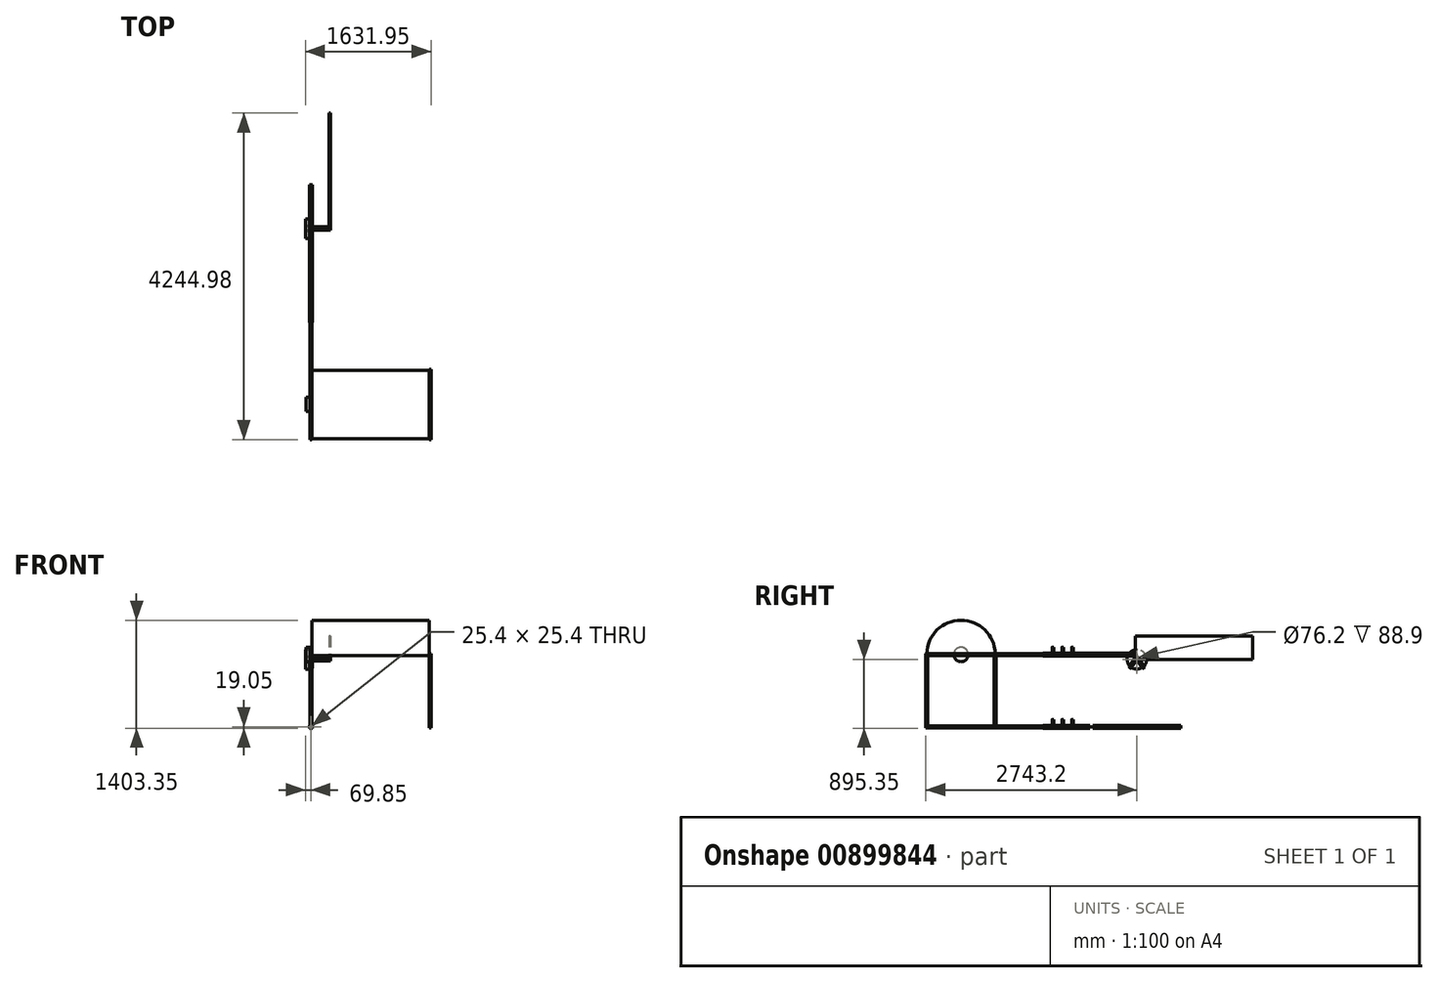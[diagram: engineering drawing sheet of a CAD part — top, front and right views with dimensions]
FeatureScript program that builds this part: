
annotation { "Feature Type Name" : "Feature", "Feature Type Description" : "" }
export const myFeature = defineFeature(function(context is Context, id is Id, definition is map)
    precondition{}
    {
        {
            var Q0;
            Q0=qCreatedBy(makeId("Top.planeOp"),FACE);
            var sketch = newSketch(context, id + "F0", { "sketchPlane" : qUnion([Q0])});
            skLineSegment(sketch, "E0.bottom", {"start": v(0, -232.23) * mm, "end": v(-25.4, -232.23) * mm});
            skLineSegment(sketch, "E0.top", {"start": v(0, 682.17) * mm, "end": v(-25.4, 682.17) * mm});
            skLineSegment(sketch, "E0.left", {"start": v(0, -232.23) * mm, "end": v(0, 682.17) * mm});
            skLineSegment(sketch, "E0.right", {"start": v(-25.4, -232.23) * mm, "end": v(-25.4, 682.17) * mm});
            skLineSegment(sketch, "E1", {"start": v(0, -232.23) * mm, "end": v(1524, -232.23) * mm});
            skLineSegment(sketch, "E2.bottom", {"start": v(1524, -232.23) * mm, "end": v(1549.4, -232.23) * mm});
            skLineSegment(sketch, "E2.top", {"start": v(1524, 682.17) * mm, "end": v(1549.4, 682.17) * mm});
            skLineSegment(sketch, "E2.left", {"start": v(1524, -232.23) * mm, "end": v(1524, 682.17) * mm});
            skLineSegment(sketch, "E2.right", {"start": v(1549.4, -232.23) * mm, "end": v(1549.4, 682.17) * mm});
            skSolve(sketch);
        }
        {
            var Q0;
            Q0=makeQuery(id+"F0.imprint","IMPRINT",FACE,{"disambiguationData":[TD([[makeQuery(id+"F0.imprint","IMPRINT",EDGE,{"derivedFrom":sQuery(id+"F0.wireOp",EDGE,"E0.bottom")}),-1.0]])]});
            var Q1;
            Q1=makeQuery(id+"F0.imprint","IMPRINT",FACE,{"disambiguationData":[TD([[makeQuery(id+"F0.imprint","IMPRINT",EDGE,{"derivedFrom":sQuery(id+"F0.wireOp",EDGE,"E2.bottom")}),1.0]])]});
            extrude(context, id + "F1", {"entities" : qUnion([Q0, Q1]), "depth" : 25.4 * mm, "offsetDistance" : 25.4 * mm});
        }
        {
            var Q0;
            Q0=makeQuery(id+"F1.opExtrude","CAP_FACE",FACE,{"disambiguationData":[OSD([sQuery(id+"F0.wireOp",EDGE,"E0.bottom"),sQuery(id+"F0.wireOp",EDGE,"E0.top"),sQuery(id+"F0.wireOp",EDGE,"E0.left"),sQuery(id+"F0.wireOp",EDGE,"E0.right")])],"isStart":false});
            var sketch = newSketch(context, id + "F2", { "sketchPlane" : qUnion([Q0])});
            skLineSegment(sketch, "E3.bottom", {"start": v(0, -232.23) * mm, "end": v(-25.4, -232.23) * mm});
            skLineSegment(sketch, "E3.top", {"start": v(0, -206.83) * mm, "end": v(-25.4, -206.83) * mm});
            skLineSegment(sketch, "E3.left", {"start": v(0, -232.23) * mm, "end": v(0, -206.83) * mm});
            skLineSegment(sketch, "E3.right", {"start": v(-25.4, -232.23) * mm, "end": v(-25.4, -206.83) * mm});
            skLineSegment(sketch, "E4.bottom", {"start": v(-25.4, 682.17) * mm, "end": v(0, 682.17) * mm});
            skLineSegment(sketch, "E4.top", {"start": v(-25.4, 656.77) * mm, "end": v(0, 656.77) * mm});
            skLineSegment(sketch, "E4.left", {"start": v(-25.4, 682.17) * mm, "end": v(-25.4, 656.77) * mm});
            skLineSegment(sketch, "E4.right", {"start": v(0, 682.17) * mm, "end": v(0, 656.77) * mm});
            skSolve(sketch);
        }
        {
            var Q0;
            Q0=makeQuery(id+"F1.opExtrude","CAP_FACE",FACE,{"disambiguationData":[OSD([sQuery(id+"F0.wireOp",EDGE,"E2.bottom"),sQuery(id+"F0.wireOp",EDGE,"E2.top"),sQuery(id+"F0.wireOp",EDGE,"E2.left"),sQuery(id+"F0.wireOp",EDGE,"E2.right")])],"isStart":false});
            var sketch = newSketch(context, id + "F3", { "sketchPlane" : qUnion([Q0])});
            skLineSegment(sketch, "E5.bottom", {"start": v(1524, 682.17) * mm, "end": v(1549.4, 682.17) * mm});
            skLineSegment(sketch, "E5.top", {"start": v(1524, 656.77) * mm, "end": v(1549.4, 656.77) * mm});
            skLineSegment(sketch, "E5.left", {"start": v(1524, 682.17) * mm, "end": v(1524, 656.77) * mm});
            skLineSegment(sketch, "E5.right", {"start": v(1549.4, 682.17) * mm, "end": v(1549.4, 656.77) * mm});
            skLineSegment(sketch, "E6.bottom", {"start": v(1549.4, -232.23) * mm, "end": v(1524, -232.23) * mm});
            skLineSegment(sketch, "E6.top", {"start": v(1549.4, -206.83) * mm, "end": v(1524, -206.83) * mm});
            skLineSegment(sketch, "E6.left", {"start": v(1549.4, -232.23) * mm, "end": v(1549.4, -206.83) * mm});
            skLineSegment(sketch, "E6.right", {"start": v(1524, -232.23) * mm, "end": v(1524, -206.83) * mm});
            skSolve(sketch);
        }
        {
            var Q0;
            Q0=makeQuery(id+"F2.imprint","IMPRINT",FACE,{"disambiguationData":[TD([[makeQuery(id+"F2.imprint","IMPRINT",EDGE,{"derivedFrom":sQuery(id+"F2.wireOp",EDGE,"E4.bottom")}),1.0]])]});
            var Q1;
            Q1=makeQuery(id+"F2.imprint","IMPRINT",FACE,{"disambiguationData":[TD([[makeQuery(id+"F2.imprint","IMPRINT",EDGE,{"derivedFrom":sQuery(id+"F2.wireOp",EDGE,"E3.bottom")}),-1.0]])]});
            var Q2;
            Q2=makeQuery(id+"F3.imprint","IMPRINT",FACE,{"disambiguationData":[TD([[makeQuery(id+"F3.imprint","IMPRINT",EDGE,{"derivedFrom":sQuery(id+"F3.wireOp",EDGE,"E6.bottom")}),1.0]])]});
            var Q3;
            Q3=makeQuery(id+"F3.imprint","IMPRINT",FACE,{"disambiguationData":[TD([[makeQuery(id+"F3.imprint","IMPRINT",EDGE,{"derivedFrom":sQuery(id+"F3.wireOp",EDGE,"E5.bottom")}),-1.0]])]});
            extrude(context, id + "F4", {"entities" : qUnion([Q0, Q1, Q2, Q3]), "depth" : 914.4 * mm, "offsetDistance" : 25.4 * mm});
        }
        {
            var Q0;
            Q0=makeQuery(id+"F4.opExtrude","CAP_FACE",FACE,{"disambiguationData":[OSD([sQuery(id+"F2.wireOp",EDGE,"E3.bottom"),sQuery(id+"F2.wireOp",EDGE,"E3.top"),sQuery(id+"F2.wireOp",EDGE,"E3.left"),sQuery(id+"F2.wireOp",EDGE,"E3.right")])],"isStart":false});
            var sketch = newSketch(context, id + "F5", { "sketchPlane" : qUnion([Q0])});
            skLineSegment(sketch, "E7.bottom", {"start": v(0, -232.23) * mm, "end": v(-25.4, -232.23) * mm});
            skLineSegment(sketch, "E7.top", {"start": v(0, 682.17) * mm, "end": v(-25.4, 682.17) * mm});
            skLineSegment(sketch, "E7.left", {"start": v(0, -232.23) * mm, "end": v(0, 682.17) * mm});
            skLineSegment(sketch, "E7.right", {"start": v(-25.4, -232.23) * mm, "end": v(-25.4, 682.17) * mm});
            skSolve(sketch);
        }
        {
            var Q0;
            Q0=makeQuery(id+"F4.opExtrude","CAP_FACE",FACE,{"disambiguationData":[OSD([sQuery(id+"F3.wireOp",EDGE,"E6.bottom"),sQuery(id+"F3.wireOp",EDGE,"E6.top"),sQuery(id+"F3.wireOp",EDGE,"E6.left"),sQuery(id+"F3.wireOp",EDGE,"E6.right")])],"isStart":false});
            var sketch = newSketch(context, id + "F6", { "sketchPlane" : qUnion([Q0])});
            skLineSegment(sketch, "E8.bottom", {"start": v(1549.4, -232.23) * mm, "end": v(1524, -232.23) * mm});
            skLineSegment(sketch, "E8.top", {"start": v(1549.4, 682.17) * mm, "end": v(1524, 682.17) * mm});
            skLineSegment(sketch, "E8.left", {"start": v(1549.4, -232.23) * mm, "end": v(1549.4, 682.17) * mm});
            skLineSegment(sketch, "E8.right", {"start": v(1524, -232.23) * mm, "end": v(1524, 682.17) * mm});
            skSolve(sketch);
        }
        {
            var Q0;
            {var subQ0=sQuery(id+"F6.wireOp",EDGE,"E8.bottom");Q0=makeQuery(id+"F6.imprint","IMPRINT",FACE,{"disambiguationData":[TD([[makeQuery(id+"F6.imprint","IMPRINT",EDGE,{"derivedFrom":subQ0}),1.0]])]});}
            var Q1;
            {var subQ0=sQuery(id+"F6.wireOp",EDGE,"E8.top");Q1=makeQuery(id+"F6.imprint","IMPRINT",FACE,{"disambiguationData":[TD([[makeQuery(id+"F6.imprint","IMPRINT",EDGE,{"derivedFrom":subQ0}),1.0]])]});}
            var Q2;
            {var subQ0=sQuery(id+"F5.wireOp",EDGE,"E7.bottom");Q2=makeQuery(id+"F5.imprint","IMPRINT",FACE,{"disambiguationData":[TD([[makeQuery(id+"F5.imprint","IMPRINT",EDGE,{"derivedFrom":subQ0}),-1.0]])]});}
            var Q3;
            {var subQ0=sQuery(id+"F5.wireOp",EDGE,"E7.top");Q3=makeQuery(id+"F5.imprint","IMPRINT",FACE,{"disambiguationData":[TD([[makeQuery(id+"F5.imprint","IMPRINT",EDGE,{"derivedFrom":subQ0}),1.0]])]});}
            extrude(context, id + "F7", {"entities" : qUnion([Q0, Q1, Q2, Q3]), "depth" : 25.4 * mm, "offsetDistance" : 25.4 * mm});
        }
        {
            var Q0;
            Q0=makeQuery(id+"F7.opExtrude","SWEPT_FACE",FACE,{"disambiguationData":[OSD([sQuery(id+"F5.wireOp",EDGE,"E7.left")])]});
            var sketch = newSketch(context, id + "F8", { "sketchPlane" : qUnion([Q0])});
            skLineSegment(sketch, "E9", {"start": v(-232.23, 965.2) * mm, "end": v(224.97, 965.2) * mm});
            skLineSegment(sketch, "E10", {"start": v(224.97, 965.2) * mm, "end": v(682.17, 965.2) * mm});
            skLineSegment(sketch, "E11", {"start": v(-232.23, 965.2) * mm, "end": v(-232.23, 952.5) * mm});
            skLineSegment(sketch, "E12", {"start": v(-232.23, 952.5) * mm, "end": v(224.97, 952.5) * mm});
            skCircle(sketch, "E13", {"center": v(224.97, 952.5) * mm, "radius": 444.5 * mm});
            skSolve(sketch);
        }
        {
            var Q0;
            {var subQ0=sQuery(id+"F8.wireOp",EDGE,"E10");var subQ1=sQuery(id+"F8.wireOp",EDGE,"E9");var subQ2=makeQuery(id+"F8.imprint","INTERSECT",VERTEX,{"derivedFrom":[subQ1,subQ0]});Q0=makeQuery(id+"F8.imprint","IMPRINT",FACE,{"disambiguationData":[TD([[makeQuery(id+"F8.imprint","IMPRINT",EDGE,{"disambiguationData":[TD([[subQ2,1.0]])],"derivedFrom":subQ1}),1.0]])]});}
            var Q1;
            {var subQ4=sQuery(id+"F8.wireOp",EDGE,"E9");var subQ6=sQuery(id+"F8.wireOp",EDGE,"E10");var subQ7=makeQuery(id+"F8.imprint","INTERSECT",VERTEX,{"derivedFrom":[subQ4,subQ6]});Q1=makeQuery(id+"F8.imprint","IMPRINT",FACE,{"disambiguationData":[TD([[makeQuery(id+"F8.imprint","IMPRINT",EDGE,{"disambiguationData":[TD([[subQ7,1.0]])],"derivedFrom":subQ4}),-1.0]])]});}
            var Q2;
            {var subQ0=sQuery(id+"F8.wireOp",EDGE,"E13");var subQ1=makeQuery(id+"F7.opExtrude","CAP_EDGE",EDGE,{"disambiguationData":[OSD([sQuery(id+"F5.wireOp",EDGE,"E7.left")])],"isStart":true});var subQ2=makeQuery(id+"F8.imprint","INTERSECT",VERTEX,{"disambiguationData":[OD(0.0)],"derivedFrom":[subQ1,subQ0]});Q2=makeQuery(id+"F8.imprint","IMPRINT",FACE,{"disambiguationData":[TD([[makeQuery(id+"F8.imprint","IMPRINT",EDGE,{"disambiguationData":[TD([[subQ2,-1.0]])],"derivedFrom":subQ0}),1.0]])]});}
            extrude(context, id + "F9", {"entities" : qUnion([Q0, Q1, Q2]), "depth" : 1524 * mm, "offsetDistance" : 25.4 * mm});
        }
        {
            var Q0;
            Q0=makeQuery(id+"F7.opExtrude","SWEPT_FACE",FACE,{"disambiguationData":[OSD([sQuery(id+"F5.wireOp",EDGE,"E7.right")])]});
            var sketch = newSketch(context, id + "F10", { "sketchPlane" : qUnion([Q0])});
            skLineSegment(sketch, "E14", {"start": v(-682.17, 939.8) * mm, "end": v(-682.17, 952.5) * mm});
            skLineSegment(sketch, "E15", {"start": v(-682.17, 952.5) * mm, "end": v(-224.97, 952.5) * mm});
            skPoint(sketch, "E15.endSnap0", {"position": v(-224.97, 939.8) * mm});
            skCircle(sketch, "E16", {"center": v(-224.97, 952.5) * mm, "radius": 93.93 * mm});
            skSolve(sketch);
        }
        {
            var Q0;
            {var subQ0=sQuery(id+"F10.wireOp",EDGE,"E16");var subQ1=makeQuery(id+"F7.opExtrude","CAP_EDGE",EDGE,{"disambiguationData":[OSD([sQuery(id+"F5.wireOp",EDGE,"E7.right")])],"isStart":false});var subQ2=makeQuery(id+"F10.imprint","INTERSECT",VERTEX,{"disambiguationData":[OD(0.0)],"derivedFrom":[subQ1,subQ0]});Q0=makeQuery(id+"F10.imprint","IMPRINT",FACE,{"disambiguationData":[TD([[makeQuery(id+"F10.imprint","IMPRINT",EDGE,{"disambiguationData":[TD([[subQ2,1.0]])],"derivedFrom":subQ0}),1.0]])]});}
            var Q1;
            {var subQ0=sQuery(id+"F10.wireOp",EDGE,"E16");var subQ7=makeQuery(id+"F10.imprint","INTERSECT",VERTEX,{"derivedFrom":[sQuery(id+"F10.wireOp",EDGE,"E15"),subQ0]});Q1=makeQuery(id+"F10.imprint","IMPRINT",FACE,{"disambiguationData":[TD([[makeQuery(id+"F10.imprint","IMPRINT",EDGE,{"disambiguationData":[TD([[subQ7,1.0]])],"derivedFrom":subQ0}),1.0]])]});}
            var Q2;
            {var subQ0=sQuery(id+"F10.wireOp",EDGE,"E16");var subQ1=makeQuery(id+"F7.opExtrude","CAP_EDGE",EDGE,{"disambiguationData":[OSD([sQuery(id+"F5.wireOp",EDGE,"E7.right")])],"isStart":true});var subQ2=makeQuery(id+"F10.imprint","INTERSECT",VERTEX,{"disambiguationData":[OD(0.0)],"derivedFrom":[subQ1,subQ0]});Q2=makeQuery(id+"F10.imprint","IMPRINT",FACE,{"disambiguationData":[TD([[makeQuery(id+"F10.imprint","IMPRINT",EDGE,{"disambiguationData":[TD([[subQ2,-1.0]])],"derivedFrom":subQ0}),1.0]])]});}
            extrude(context, id + "F11", {"entities" : qUnion([Q0, Q1, Q2]), "operationType" : NewBodyOperationType.ADD, "depth" : 50.8 * mm, "offsetDistance" : 25.4 * mm});
        }
        {
            var Q0;
            Q0=makeQuery(id+"F1.opExtrude","SWEPT_FACE",FACE,{"disambiguationData":[OSD([sQuery(id+"F0.wireOp",EDGE,"E0.top")])]});
            extrude(context, id + "F12", {"entities" : qUnion([Q0]), "operationType" : NewBodyOperationType.ADD, "depth" : 609.6 * mm, "offsetDistance" : 25.4 * mm});
        }
        {
            var Q0;
            Q0=makeQuery(id+"F7.opExtrude","SWEPT_FACE",FACE,{"disambiguationData":[OSD([sQuery(id+"F5.wireOp",EDGE,"E7.top")])]});
            extrude(context, id + "F13", {"entities" : qUnion([Q0]), "operationType" : NewBodyOperationType.ADD, "depth" : 609.6 * mm, "offsetDistance" : 25.4 * mm});
        }
        {
            var Q0;
            Q0=makeQuery(id+"F13.opExtrude","CAP_FACE",FACE,{"disambiguationData":[OSD([sQuery(id+"F5.wireOp",EDGE,"E7.top")])],"isStart":false});
            var sketch = newSketch(context, id + "F14", { "sketchPlane" : qUnion([Q0])});
            skLineSegment(sketch, "E17", {"start": v(0, 952.5) * mm, "end": v(25.4, 952.5) * mm});
            skLineSegment(sketch, "E18", {"start": v(25.4, 952.5) * mm, "end": v(25.4, 939.8) * mm});
            skLineSegment(sketch, "E19", {"start": v(12.7, 939.8) * mm, "end": v(12.7, 965.2) * mm});
            skLineSegment(sketch, "E20.bottom", {"start": v(12.7, 952.5) * mm, "end": v(31.75, 952.5) * mm});
            skLineSegment(sketch, "E20.top", {"start": v(12.7, 971.55) * mm, "end": v(31.75, 971.55) * mm});
            skLineSegment(sketch, "E20.left", {"start": v(12.7, 952.5) * mm, "end": v(12.7, 971.55) * mm});
            skLineSegment(sketch, "E20.right", {"start": v(31.75, 952.5) * mm, "end": v(31.75, 971.55) * mm});
            skLineSegment(sketch, "E21.bottom", {"start": v(12.7, 952.5) * mm, "end": v(-6.35, 952.5) * mm});
            skLineSegment(sketch, "E21.top", {"start": v(12.7, 971.55) * mm, "end": v(-6.35, 971.55) * mm});
            skLineSegment(sketch, "E21.right", {"start": v(-6.35, 952.5) * mm, "end": v(-6.35, 971.55) * mm});
            skLineSegment(sketch, "E22.bottom", {"start": v(12.7, 952.5) * mm, "end": v(41.68, 952.5) * mm});
            skLineSegment(sketch, "E23.bottom", {"start": v(12.7, 952.5) * mm, "end": v(-25.57, 952.5) * mm});
            skLineSegment(sketch, "E24.bottom", {"start": v(-6.35, 952.5) * mm, "end": v(12.7, 952.5) * mm});
            skLineSegment(sketch, "E24.top", {"start": v(-6.35, 933.45) * mm, "end": v(12.7, 933.45) * mm});
            skLineSegment(sketch, "E24.left", {"start": v(-6.35, 952.5) * mm, "end": v(-6.35, 933.45) * mm});
            skLineSegment(sketch, "E24.right", {"start": v(12.7, 952.5) * mm, "end": v(12.7, 933.45) * mm});
            skLineSegment(sketch, "E25.top", {"start": v(12.7, 933.45) * mm, "end": v(31.75, 933.45) * mm});
            skLineSegment(sketch, "E25.right", {"start": v(31.75, 952.5) * mm, "end": v(31.75, 933.45) * mm});
            skSolve(sketch);
        }
        {
            var Q0;
            {var subQ6=sQuery(id+"F14.wireOp",EDGE,"E21.top");Q0=makeQuery(id+"F14.imprint","IMPRINT",FACE,{"disambiguationData":[TD([[makeQuery(id+"F14.imprint","IMPRINT",EDGE,{"derivedFrom":subQ6}),1.0]])]});}
            var Q1;
            {var subQ1=sQuery(id+"F14.wireOp",EDGE,"E20.top");Q1=makeQuery(id+"F14.imprint","IMPRINT",FACE,{"disambiguationData":[TD([[makeQuery(id+"F14.imprint","IMPRINT",EDGE,{"derivedFrom":subQ1}),-1.0]])]});}
            var Q2;
            {var subQ2=sQuery(id+"F14.wireOp",EDGE,"E18");Q2=makeQuery(id+"F14.imprint","IMPRINT",FACE,{"disambiguationData":[TD([[makeQuery(id+"F14.imprint","IMPRINT",EDGE,{"derivedFrom":subQ2}),1.0]])]});}
            var Q3;
            {var subQ1=sQuery(id+"F14.wireOp",EDGE,"E24.top");Q3=makeQuery(id+"F14.imprint","IMPRINT",FACE,{"disambiguationData":[TD([[makeQuery(id+"F14.imprint","IMPRINT",EDGE,{"derivedFrom":subQ1}),1.0]])]});}
            extrude(context, id + "F15", {"entities" : qUnion([Q0, Q1, Q2, Q3]), "depth" : 1219.2 * mm, "offsetDistance" : 25.4 * mm});
        }
        {
            var Q0;
            Q0=makeQuery(id+"F12.opExtrude","CAP_FACE",FACE,{"disambiguationData":[OSD([sQuery(id+"F0.wireOp",EDGE,"E0.top")])],"isStart":false});
            var sketch = newSketch(context, id + "F16", { "sketchPlane" : qUnion([Q0])});
            skLineSegment(sketch, "E26", {"start": v(0, 25.4) * mm, "end": v(12.7, 25.4) * mm});
            skLineSegment(sketch, "E27", {"start": v(12.7, 25.4) * mm, "end": v(12.7, 12.7) * mm});
            skPoint(sketch, "E27.endSnap0", {"position": v(0, 12.7) * mm});
            skLineSegment(sketch, "E28", {"start": v(12.7, 12.7) * mm, "end": v(0, 12.7) * mm});
            skLineSegment(sketch, "E29.bottom", {"start": v(12.7, 12.7) * mm, "end": v(-6.35, 12.7) * mm});
            skLineSegment(sketch, "E29.top", {"start": v(12.7, 31.75) * mm, "end": v(-6.35, 31.75) * mm});
            skLineSegment(sketch, "E29.left", {"start": v(12.7, 12.7) * mm, "end": v(12.7, 31.75) * mm});
            skLineSegment(sketch, "E29.right", {"start": v(-6.35, 12.7) * mm, "end": v(-6.35, 31.75) * mm});
            skLineSegment(sketch, "E30.bottom", {"start": v(12.7, 12.7) * mm, "end": v(31.75, 12.7) * mm});
            skLineSegment(sketch, "E30.top", {"start": v(12.7, -6.35) * mm, "end": v(31.75, -6.35) * mm});
            skLineSegment(sketch, "E30.left", {"start": v(12.7, 12.7) * mm, "end": v(12.7, -6.35) * mm});
            skLineSegment(sketch, "E30.right", {"start": v(31.75, 12.7) * mm, "end": v(31.75, -6.35) * mm});
            skLineSegment(sketch, "E31.top", {"start": v(12.7, 31.75) * mm, "end": v(31.75, 31.75) * mm});
            skLineSegment(sketch, "E31.right", {"start": v(31.75, 12.7) * mm, "end": v(31.75, 31.75) * mm});
            skLineSegment(sketch, "E32.top", {"start": v(12.7, -6.35) * mm, "end": v(-6.35, -6.35) * mm});
            skLineSegment(sketch, "E32.right", {"start": v(-6.35, 12.7) * mm, "end": v(-6.35, -6.35) * mm});
            skSolve(sketch);
        }
        {
            var Q0;
            {var subQ1=sQuery(id+"F16.wireOp",EDGE,"E26");Q0=makeQuery(id+"F16.imprint","IMPRINT",FACE,{"disambiguationData":[TD([[makeQuery(id+"F16.imprint","IMPRINT",EDGE,{"derivedFrom":subQ1}),1.0]])]});}
            var Q1;
            {var subQ9=sQuery(id+"F16.wireOp",EDGE,"E31.top");Q1=makeQuery(id+"F16.imprint","IMPRINT",FACE,{"disambiguationData":[TD([[makeQuery(id+"F16.imprint","IMPRINT",EDGE,{"derivedFrom":subQ9}),-1.0]])]});}
            var Q2;
            {var subQ1=sQuery(id+"F16.wireOp",EDGE,"E30.top");Q2=makeQuery(id+"F16.imprint","IMPRINT",FACE,{"disambiguationData":[TD([[makeQuery(id+"F16.imprint","IMPRINT",EDGE,{"derivedFrom":subQ1}),1.0]])]});}
            var Q3;
            {var subQ2=sQuery(id+"F16.wireOp",EDGE,"E32.top");Q3=makeQuery(id+"F16.imprint","IMPRINT",FACE,{"disambiguationData":[TD([[makeQuery(id+"F16.imprint","IMPRINT",EDGE,{"derivedFrom":subQ2}),-1.0]])]});}
            extrude(context, id + "F17", {"entities" : qUnion([Q0, Q1, Q2, Q3]), "depth" : 609.6 * mm, "offsetDistance" : 25.4 * mm});
        }
        {
            var Q0;
            Q0=makeQuery(id+"F17.opExtrude","SWEPT_FACE",FACE,{"disambiguationData":[OSD([sQuery(id+"F16.wireOp",EDGE,"E30.right"),sQuery(id+"F16.wireOp",EDGE,"E31.right")])]});
            var sketch = newSketch(context, id + "F18", { "sketchPlane" : qUnion([Q0])});
            skLineSegment(sketch, "E33", {"start": v(-1901.37, -6.35) * mm, "end": v(-1901.37, 31.75) * mm});
            skLineSegment(sketch, "E34", {"start": v(-1901.37, 31.75) * mm, "end": v(-3120.57, 31.75) * mm});
            skLineSegment(sketch, "E35", {"start": v(-3120.57, 31.75) * mm, "end": v(-3120.57, -6.35) * mm});
            skLineSegment(sketch, "E36", {"start": v(-3120.57, -6.35) * mm, "end": v(-1901.37, -6.35) * mm});
            skLineSegment(sketch, "E37", {"start": v(-3120.57, 31.75) * mm, "end": v(-2510.97, 31.75) * mm});
            skLineSegment(sketch, "E38", {"start": v(-2510.97, 31.75) * mm, "end": v(-2510.97, 946.15) * mm});
            skCircle(sketch, "E39", {"center": v(-2510.97, 946.15) * mm, "radius": 190.5 * mm});
            skLineSegment(sketch, "E40.bottom", {"start": v(-1901.37, -6.35) * mm, "end": v(-1939.47, -6.35) * mm});
            skLineSegment(sketch, "E40.top", {"start": v(-1901.37, 31.75) * mm, "end": v(-1939.47, 31.75) * mm});
            skLineSegment(sketch, "E40.right", {"start": v(-1939.47, -6.35) * mm, "end": v(-1939.47, 31.75) * mm});
            skLineSegment(sketch, "E41.bottom", {"start": v(-3120.57, -6.35) * mm, "end": v(-3082.47, -6.35) * mm});
            skLineSegment(sketch, "E41.top", {"start": v(-3120.57, 31.75) * mm, "end": v(-3082.47, 31.75) * mm});
            skLineSegment(sketch, "E41.left", {"start": v(-3120.57, -6.35) * mm, "end": v(-3120.57, 31.75) * mm});
            skLineSegment(sketch, "E41.right", {"start": v(-3082.47, -6.35) * mm, "end": v(-3082.47, 31.75) * mm});
            skLineSegment(sketch, "E42", {"start": v(-3120.57, 31.75) * mm, "end": v(-2510.97, 946.15) * mm});
            skLineSegment(sketch, "E43", {"start": v(-1901.37, 31.75) * mm, "end": v(-2510.97, 946.15) * mm});
            skLineSegment(sketch, "E44", {"start": v(-1939.47, 31.75) * mm, "end": v(-2510.97, 889) * mm});
            skLineSegment(sketch, "E45", {"start": v(-2510.97, 889) * mm, "end": v(-3082.47, 31.75) * mm});
            skSolve(sketch);
        }
        {
            var Q0;
            {var subQ5=sQuery(id+"F18.wireOp",EDGE,"E40.top");Q0=makeQuery(id+"F18.imprint","IMPRINT",FACE,{"disambiguationData":[TD([[makeQuery(id+"F18.imprint","IMPRINT",EDGE,{"derivedFrom":subQ5}),-1.0]])]});}
            var Q1;
            {var subQ0=sQuery(id+"F18.wireOp",EDGE,"E43");var subQ5=sQuery(id+"F18.wireOp",EDGE,"E39");var subQ6=makeQuery(id+"F18.imprint","INTERSECT",VERTEX,{"derivedFrom":[subQ5,subQ0]});Q1=makeQuery(id+"F18.imprint","IMPRINT",FACE,{"disambiguationData":[TD([[makeQuery(id+"F18.imprint","IMPRINT",EDGE,{"disambiguationData":[TD([[subQ6,1.0]])],"derivedFrom":subQ5}),1.0]])]});}
            var Q2;
            {var subQ5=sQuery(id+"F18.wireOp",EDGE,"E41.top");Q2=makeQuery(id+"F18.imprint","IMPRINT",FACE,{"disambiguationData":[TD([[makeQuery(id+"F18.imprint","IMPRINT",EDGE,{"derivedFrom":subQ5}),1.0]])]});}
            var Q3;
            {var subQ0=sQuery(id+"F18.wireOp",EDGE,"E42");var subQ5=sQuery(id+"F18.wireOp",EDGE,"E39");var subQ6=makeQuery(id+"F18.imprint","INTERSECT",VERTEX,{"derivedFrom":[subQ5,subQ0]});Q3=makeQuery(id+"F18.imprint","IMPRINT",FACE,{"disambiguationData":[TD([[makeQuery(id+"F18.imprint","IMPRINT",EDGE,{"disambiguationData":[TD([[subQ6,-1.0]])],"derivedFrom":subQ5}),1.0]])]});}
            var Q4;
            Q4=makeQuery(id+"F18.imprint","IMPRINT",FACE,{"disambiguationData":[TD([[makeQuery(id+"F18.imprint","IMPRINT",EDGE,{"derivedFrom":sQuery(id+"F18.wireOp",EDGE,"E34")}),1.0]])]});
            var Q5;
            Q5=makeQuery(id+"F18.imprint","IMPRINT",FACE,{"disambiguationData":[TD([[makeQuery(id+"F18.imprint","IMPRINT",EDGE,{"derivedFrom":sQuery(id+"F18.wireOp",EDGE,"E40.bottom")}),-1.0]])]});
            var Q6;
            Q6=makeQuery(id+"F18.imprint","IMPRINT",FACE,{"disambiguationData":[TD([[makeQuery(id+"F18.imprint","IMPRINT",EDGE,{"derivedFrom":sQuery(id+"F18.wireOp",EDGE,"E41.bottom")}),1.0]])]});
            extrude(context, id + "F19", {"entities" : qUnion([Q0, Q1, Q2, Q3, Q4, Q5, Q6]), "operationType" : NewBodyOperationType.ADD, "depth" : -38.1 * mm, "offsetDistance" : 25.4 * mm});
        }
        {
            var Q0;
            Q0=makeQuery(id+"F19.boolean.opBoolean","MERGE",FACE,{"derivedFrom":[makeQuery(id+"F15.opExtrude","SWEPT_FACE",FACE,{"disambiguationData":[OSD([sQuery(id+"F14.wireOp",EDGE,"E20.right"),sQuery(id+"F14.wireOp",EDGE,"E25.right")])]}),makeQuery(id+"F19.opExtrude","CAP_FACE",FACE,{"disambiguationData":[OSD([sQuery(id+"F18.wireOp",EDGE,"E34"),sQuery(id+"F18.wireOp",EDGE,"E36"),sQuery(id+"F18.wireOp",EDGE,"E37"),sQuery(id+"F18.wireOp",EDGE,"E40.bottom"),sQuery(id+"F18.wireOp",EDGE,"E33"),sQuery(id+"F18.wireOp",EDGE,"E41.bottom"),sQuery(id+"F18.wireOp",EDGE,"E41.left"),sQuery(id+"F18.wireOp",EDGE,"E42"),sQuery(id+"F18.wireOp",EDGE,"E43"),sQuery(id+"F18.wireOp",EDGE,"E44"),sQuery(id+"F18.wireOp",EDGE,"E45")])],"isStart":true})]});
            var sketch = newSketch(context, id + "F20", { "sketchPlane" : qUnion([Q0])});
            skCircle(sketch, "E46", {"center": v(-2510.97, 889) * mm, "radius": 127 * mm});
            skSolve(sketch);
        }
        {
            var Q0;
            {var subQ1=sQuery(id+"F14.wireOp",EDGE,"E20.right");var subQ6=makeQuery(id+"F15.opExtrude","CAP_EDGE",EDGE,{"disambiguationData":[OSD([subQ1,sQuery(id+"F14.wireOp",EDGE,"E25.right")])],"isStart":false});Q0=makeQuery(id+"F20.imprint","IMPRINT",FACE,{"disambiguationData":[TD([[makeQuery(id+"F20.imprint","IMPRINT",EDGE,{"derivedFrom":subQ6}),1.0]])]});}
            var Q1;
            {var subQ0=sQuery(id+"F14.wireOp",EDGE,"E25.right");var subQ1=sQuery(id+"F14.wireOp",EDGE,"E20.right");var subQ2=makeQuery(id+"F15.opExtrude","CAP_EDGE",EDGE,{"disambiguationData":[OSD([subQ1,subQ0])],"isStart":false});Q1=makeQuery(id+"F20.imprint","IMPRINT",FACE,{"disambiguationData":[TD([[makeQuery(id+"F20.imprint","IMPRINT",EDGE,{"derivedFrom":subQ2}),-1.0]])]});}
            var Q2;
            {var subQ0=sQuery(id+"F20.wireOp",EDGE,"E46");var subQ3=makeQuery(id+"F19.opExtrude","CAP_EDGE",EDGE,{"disambiguationData":[OSD([sQuery(id+"F18.wireOp",EDGE,"E43")])],"isStart":true});var subQ4=makeQuery(id+"F20.imprint","INTERSECT",VERTEX,{"derivedFrom":[subQ3,subQ0]});Q2=makeQuery(id+"F20.imprint","IMPRINT",FACE,{"disambiguationData":[TD([[makeQuery(id+"F20.imprint","IMPRINT",EDGE,{"disambiguationData":[TD([[subQ4,-1.0]])],"derivedFrom":subQ0}),1.0]])]});}
            var Q3;
            {var subQ0=sQuery(id+"F20.wireOp",EDGE,"E46");var subQ1=makeQuery(id+"F19.opExtrude","CAP_EDGE",EDGE,{"disambiguationData":[OSD([sQuery(id+"F18.wireOp",EDGE,"E45")])],"isStart":true});var subQ2=makeQuery(id+"F20.imprint","INTERSECT",VERTEX,{"derivedFrom":[subQ1,subQ0]});Q3=makeQuery(id+"F20.imprint","IMPRINT",FACE,{"disambiguationData":[TD([[makeQuery(id+"F20.imprint","IMPRINT",EDGE,{"disambiguationData":[TD([[subQ2,-1.0]])],"derivedFrom":subQ0}),1.0]])]});}
            extrude(context, id + "F21", {"entities" : qUnion([Q0, Q1, Q2, Q3]), "operationType" : NewBodyOperationType.ADD, "depth" : 50.8 * mm, "offsetDistance" : 25.4 * mm});
        }
        {
            var Q0;
            Q0=makeQuery(id+"F21.opExtrude","CAP_FACE",FACE,{"disambiguationData":[OSD([sQuery(id+"F20.wireOp",EDGE,"E46")])],"isStart":false});
            var sketch = newSketch(context, id + "F22", { "sketchPlane" : qUnion([Q0])});
            skCircle(sketch, "E47", {"center": v(-2510.97, 889) * mm, "radius": 38.1 * mm});
            skSolve(sketch);
        }
        {
            var Q0;
            Q0=sQuery(id+"F22.wireOp",VERTEX,"E47.center");
            var Q1;
            Q1=makeQuery(id+"F15.opExtrude","SWEPT_BODY",BODY,{"disambiguationData":[OSD([sQuery(id+"F5.wireOp",EDGE,"E7.top"),sQuery(id+"F5.wireOp",EDGE,"E7.left"),sQuery(id+"F5.wireOp",EDGE,"E7.right"),sQuery(id+"F14.wireOp",EDGE,"E18"),sQuery(id+"F14.wireOp",EDGE,"E20.top"),sQuery(id+"F14.wireOp",EDGE,"E20.right"),sQuery(id+"F14.wireOp",EDGE,"E21.top"),sQuery(id+"F14.wireOp",EDGE,"E21.right"),sQuery(id+"F14.wireOp",EDGE,"E24.top"),sQuery(id+"F14.wireOp",EDGE,"E24.left"),sQuery(id+"F14.wireOp",EDGE,"E25.top"),sQuery(id+"F14.wireOp",EDGE,"E25.right")])]});
            hole(context, id + "F23", {"style" : HoleStyle.SIMPLE, "endStyle" : HoleEndStyle.THROUGH, "holeDiameter" : 76.2 * mm, "majorDiameter" : 6.35 * mm, "isTappedThrough" : true, "tappedDepth" : 12.7 * mm, "tapClearance" : 3, "locations" : qUnion([Q0]), "scope" : qUnion([Q1])});
        }
        {
            var Q0;
            Q0=makeQuery(id+"F21.opExtrude","CAP_FACE",FACE,{"disambiguationData":[OSD([sQuery(id+"F20.wireOp",EDGE,"E46")])],"isStart":false});
            var sketch = newSketch(context, id + "F24", { "sketchPlane" : qUnion([Q0])});
            skCircle(sketch, "E48", {"center": v(-2510.97, 889) * mm, "radius": 22.22 * mm});
            skSolve(sketch);
        }
        {
            var Q0;
            Q0=makeQuery(id+"F24.imprint","IMPRINT",FACE,{"disambiguationData":[TD([[makeQuery(id+"F24.imprint","IMPRINT",EDGE,{"derivedFrom":sQuery(id+"F24.wireOp",EDGE,"E48")}),1.0]])]});
            extrude(context, id + "F25", {"entities" : qUnion([Q0]), "depth" : -304.8 * mm, "offsetDistance" : 25.4 * mm});
        }
        {
            var Q0;
            Q0=makeQuery(id+"F25.opExtrude","CAP_FACE",FACE,{"disambiguationData":[OSD([sQuery(id+"F24.wireOp",EDGE,"E48")])],"isStart":false});
            var sketch = newSketch(context, id + "F26", { "sketchPlane" : qUnion([Q0])});
            skLineSegment(sketch, "E49", {"start": v(2510.97, 889) * mm, "end": v(2533.2, 889) * mm});
            skLineSegment(sketch, "E50", {"start": v(2533.2, 889) * mm, "end": v(2488.75, 889) * mm});
            skSolve(sketch);
        }
        {
            var Q0;
            {var subQ0=sQuery(id+"F26.wireOp",EDGE,"E50");var subQ3=makeQuery(id+"F26.imprint","IMPRINT",VERTEX,{"derivedFrom":subQ0});Q0=makeQuery(id+"F26.imprint","IMPRINT",FACE,{"disambiguationData":[TD([[makeQuery(id+"F26.imprint","IMPRINT",EDGE,{"disambiguationData":[TD([[subQ3,1.0]])],"derivedFrom":subQ0}),1.0]])]});}
            extrude(context, id + "F27", {"entities" : qUnion([Q0]), "operationType" : NewBodyOperationType.ADD, "depth" : 22.86 * mm, "offsetDistance" : 25.4 * mm});
        }
        {
            var Q0;
            Q0=makeQuery(id+"F27.opExtrude","SWEPT_FACE",FACE,{"disambiguationData":[OSD([sQuery(id+"F26.wireOp",EDGE,"E50")])]});
            extrude(context, id + "F28", {"entities" : qUnion([Q0]), "operationType" : NewBodyOperationType.ADD, "depth" : 304.8 * mm, "offsetDistance" : 25.4 * mm});
        }
        {
            var Q0;
            {var subQ0=sQuery(id+"F26.wireOp",EDGE,"E50");Q0=makeQuery(id+"F28.opExtrude","SWEPT_FACE",FACE,{"disambiguationData":[OSD([subQ0]),TDD([makeQuery(id+"F27.opExtrude","CAP_EDGE",EDGE,{"disambiguationData":[OSD([subQ0])],"isStart":true})])]});}
            var sketch = newSketch(context, id + "F29", { "sketchPlane" : qUnion([Q0])});
            skCircle(sketch, "E51", {"center": v(-2510.97, 1193.8) * mm, "radius": 22.23 * mm});
            skSolve(sketch);
        }
        {
            var Q0;
            {var subQ1=sQuery(id+"F26.wireOp",EDGE,"E50");var subQ2=makeQuery(id+"F28.opExtrude","CAP_EDGE",EDGE,{"disambiguationData":[OSD([subQ1]),TDD([makeQuery(id+"F27.opExtrude","CAP_EDGE",EDGE,{"disambiguationData":[OSD([subQ1])],"isStart":true})])],"isStart":false});Q0=makeQuery(id+"F29.imprint","IMPRINT",FACE,{"disambiguationData":[TD([[makeQuery(id+"F29.imprint","IMPRINT",EDGE,{"derivedFrom":subQ2}),-1.0]])]});}
            var Q1;
            {var subQ1=sQuery(id+"F26.wireOp",EDGE,"E50");var subQ2=makeQuery(id+"F28.opExtrude","CAP_EDGE",EDGE,{"disambiguationData":[OSD([subQ1]),TDD([makeQuery(id+"F27.opExtrude","CAP_EDGE",EDGE,{"disambiguationData":[OSD([subQ1])],"isStart":true})])],"isStart":false});Q1=makeQuery(id+"F29.imprint","IMPRINT",FACE,{"disambiguationData":[TD([[makeQuery(id+"F29.imprint","IMPRINT",EDGE,{"derivedFrom":subQ2}),1.0]])]});}
            extrude(context, id + "F30", {"entities" : qUnion([Q0, Q1]), "operationType" : NewBodyOperationType.ADD, "depth" : -1524 * mm, "offsetDistance" : 25.4 * mm});
        }
        {
            var Q0;
            Q0=makeQuery(id+"F15.opExtrude","SWEPT_FACE",FACE,{"disambiguationData":[OSD([sQuery(id+"F14.wireOp",EDGE,"E20.top"),sQuery(id+"F14.wireOp",EDGE,"E21.top")])]});
            var sketch = newSketch(context, id + "F31", { "sketchPlane" : qUnion([Q0])});
            skLineSegment(sketch, "E52", {"start": v(-12.7, 1291.77) * mm, "end": v(-12.7, 1418.77) * mm});
            skLineSegment(sketch, "E53", {"start": v(-12.7, 1418.77) * mm, "end": v(-12.7, 1545.77) * mm});
            skLineSegment(sketch, "E54", {"start": v(-12.7, 1545.77) * mm, "end": v(-12.7, 1672.77) * mm});
            skCircle(sketch, "E55", {"center": v(-12.7, 1418.77) * mm, "radius": 9.53 * mm});
            skCircle(sketch, "E56", {"center": v(-12.7, 1545.77) * mm, "radius": 9.53 * mm});
            skCircle(sketch, "E57", {"center": v(-12.7, 1672.77) * mm, "radius": 9.53 * mm});
            skSolve(sketch);
        }
        {
            var Q0;
            {var subQ0=sQuery(id+"F31.wireOp",EDGE,"E53");var subQ1=sQuery(id+"F31.wireOp",EDGE,"E52");var subQ2=makeQuery(id+"F31.imprint","INTERSECT",VERTEX,{"derivedFrom":[subQ1,subQ0]});Q0=makeQuery(id+"F31.imprint","IMPRINT",FACE,{"disambiguationData":[TD([[makeQuery(id+"F31.imprint","IMPRINT",EDGE,{"disambiguationData":[TD([[subQ2,1.0]])],"derivedFrom":subQ1}),1.0]])]});}
            var Q1;
            {var subQ0=sQuery(id+"F31.wireOp",EDGE,"E53");var subQ1=sQuery(id+"F31.wireOp",EDGE,"E52");var subQ2=makeQuery(id+"F31.imprint","INTERSECT",VERTEX,{"derivedFrom":[subQ1,subQ0]});Q1=makeQuery(id+"F31.imprint","IMPRINT",FACE,{"disambiguationData":[TD([[makeQuery(id+"F31.imprint","IMPRINT",EDGE,{"disambiguationData":[TD([[subQ2,1.0]])],"derivedFrom":subQ1}),-1.0]])]});}
            var Q2;
            {var subQ0=sQuery(id+"F31.wireOp",EDGE,"E54");var subQ1=sQuery(id+"F31.wireOp",EDGE,"E53");var subQ2=makeQuery(id+"F31.imprint","INTERSECT",VERTEX,{"derivedFrom":[subQ1,subQ0]});Q2=makeQuery(id+"F31.imprint","IMPRINT",FACE,{"disambiguationData":[TD([[makeQuery(id+"F31.imprint","IMPRINT",EDGE,{"disambiguationData":[TD([[subQ2,1.0]])],"derivedFrom":subQ1}),1.0]])]});}
            var Q3;
            {var subQ0=sQuery(id+"F31.wireOp",EDGE,"E54");var subQ1=sQuery(id+"F31.wireOp",EDGE,"E53");var subQ2=makeQuery(id+"F31.imprint","INTERSECT",VERTEX,{"derivedFrom":[subQ1,subQ0]});Q3=makeQuery(id+"F31.imprint","IMPRINT",FACE,{"disambiguationData":[TD([[makeQuery(id+"F31.imprint","IMPRINT",EDGE,{"disambiguationData":[TD([[subQ2,1.0]])],"derivedFrom":subQ1}),-1.0]])]});}
            var Q4;
            Q4=makeQuery(id+"F31.imprint","IMPRINT",FACE,{"disambiguationData":[TD([[makeQuery(id+"F31.imprint","IMPRINT",EDGE,{"derivedFrom":sQuery(id+"F31.wireOp",EDGE,"E57")}),1.0]])]});
            extrude(context, id + "F32", {"entities" : qUnion([Q0, Q1, Q2, Q3, Q4]), "operationType" : NewBodyOperationType.ADD, "depth" : 76.2 * mm, "offsetDistance" : 25.4 * mm});
        }
        {
            var Q0;
            Q0=makeQuery(id+"F17.opExtrude","SWEPT_FACE",FACE,{"disambiguationData":[OSD([sQuery(id+"F16.wireOp",EDGE,"E29.top"),sQuery(id+"F16.wireOp",EDGE,"E31.top")])]});
            var sketch = newSketch(context, id + "F33", { "sketchPlane" : qUnion([Q0])});
            skLineSegment(sketch, "E58", {"start": v(-12.7, 1291.77) * mm, "end": v(-12.7, 1418.77) * mm});
            skLineSegment(sketch, "E59", {"start": v(-12.7, 1418.77) * mm, "end": v(-12.7, 1545.77) * mm});
            skLineSegment(sketch, "E60", {"start": v(-12.7, 1545.77) * mm, "end": v(-12.7, 1672.77) * mm});
            skCircle(sketch, "E61", {"center": v(-12.7, 1418.77) * mm, "radius": 9.53 * mm});
            skCircle(sketch, "E62", {"center": v(-12.7, 1545.77) * mm, "radius": 9.53 * mm});
            skCircle(sketch, "E63", {"center": v(-12.7, 1672.77) * mm, "radius": 9.53 * mm});
            skSolve(sketch);
        }
        {
            var Q0;
            Q0=makeQuery(id+"F33.imprint","IMPRINT",FACE,{"disambiguationData":[TD([[makeQuery(id+"F33.imprint","IMPRINT",EDGE,{"derivedFrom":sQuery(id+"F33.wireOp",EDGE,"E63")}),1.0]])]});
            var Q1;
            {var subQ0=sQuery(id+"F33.wireOp",EDGE,"E59");var subQ1=sQuery(id+"F33.wireOp",EDGE,"E58");var subQ2=makeQuery(id+"F33.imprint","INTERSECT",VERTEX,{"derivedFrom":[subQ1,subQ0]});Q1=makeQuery(id+"F33.imprint","IMPRINT",FACE,{"disambiguationData":[TD([[makeQuery(id+"F33.imprint","IMPRINT",EDGE,{"disambiguationData":[TD([[subQ2,1.0]])],"derivedFrom":subQ1}),-1.0]])]});}
            var Q2;
            {var subQ0=sQuery(id+"F33.wireOp",EDGE,"E60");var subQ1=sQuery(id+"F33.wireOp",EDGE,"E59");var subQ2=makeQuery(id+"F33.imprint","INTERSECT",VERTEX,{"derivedFrom":[subQ1,subQ0]});Q2=makeQuery(id+"F33.imprint","IMPRINT",FACE,{"disambiguationData":[TD([[makeQuery(id+"F33.imprint","IMPRINT",EDGE,{"disambiguationData":[TD([[subQ2,1.0]])],"derivedFrom":subQ1}),-1.0]])]});}
            var Q3;
            {var subQ0=sQuery(id+"F33.wireOp",EDGE,"E60");var subQ1=sQuery(id+"F33.wireOp",EDGE,"E59");var subQ2=makeQuery(id+"F33.imprint","INTERSECT",VERTEX,{"derivedFrom":[subQ1,subQ0]});Q3=makeQuery(id+"F33.imprint","IMPRINT",FACE,{"disambiguationData":[TD([[makeQuery(id+"F33.imprint","IMPRINT",EDGE,{"disambiguationData":[TD([[subQ2,1.0]])],"derivedFrom":subQ1}),1.0]])]});}
            var Q4;
            {var subQ0=sQuery(id+"F33.wireOp",EDGE,"E59");var subQ1=sQuery(id+"F33.wireOp",EDGE,"E58");var subQ2=makeQuery(id+"F33.imprint","INTERSECT",VERTEX,{"derivedFrom":[subQ1,subQ0]});Q4=makeQuery(id+"F33.imprint","IMPRINT",FACE,{"disambiguationData":[TD([[makeQuery(id+"F33.imprint","IMPRINT",EDGE,{"disambiguationData":[TD([[subQ2,1.0]])],"derivedFrom":subQ1}),1.0]])]});}
            extrude(context, id + "F34", {"entities" : qUnion([Q0, Q1, Q2, Q3, Q4]), "operationType" : NewBodyOperationType.ADD, "depth" : 76.2 * mm, "offsetDistance" : 25.4 * mm});
        }
    });
